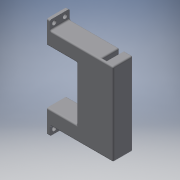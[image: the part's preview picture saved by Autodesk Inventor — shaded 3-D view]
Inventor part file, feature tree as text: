
AUTODESK INVENTOR PART (.ipt)
format: ipt  version: 2018 (Build 220112000, 112)  size: 440,320 bytes
history: native  units: in
note: dims shown in document units (in); Inventor stores cm internally (conversion verified against a paired STEP export)
features: reference x20, extrude x10, sketch x10, other x10, fillet x8, projected_geometry x4, plane x3
ambient origin geometry x8: Origin, YZ Plane, XZ Plane, XY Plane, X Axis, Y Axis, Z Axis, Center Point
bodies: Solid1 (feature_tree)
feature tree (65):
  extrude  "Extrusion1"  Depth=0.125in
  extrude  "Extrusion2"  Depth=0.4724in TaperAngle=0.0deg
  extrude  "Extrusion3"  Depth=0.2in TaperAngle=0.0deg
  extrude  "Extrusion4"  Depth=0.4in
  extrude  "Extrusion5"  Depth=0.25in
  extrude  "Extrusion6"  Depth=0.0787in TaperAngle=0.0deg
  fillet  "Fillet1"  Radius=0.125in
  fillet  "Fillet4"  Radius=0.1181in
  sketch  "Sketch8"  dims[d19=0.125in d20=0.1181in]
  plane  "Work Plane1"
  extrude  "Extrusion7"  Depth=0.1181in
  sketch  "Sketch9"  dims[d21=1.15in d22=0.0787in d23=0.0in d24=0.0394in d27=0.0394in d28=0.0197in d29=0.0197in]
  plane  "Work Plane2"
  extrude  "Extrusion8"  Depth=0.0394in TaperAngle=0.0deg
  fillet  "Fillet5"  Radius=0.0394in
  fillet  "Fillet6"  Radius=0.0394in
  fillet  "Fillet7"  Radius=0.0197in
  fillet  "Fillet9"  Radius=0.0197in
  sketch  "Sketch10"  dims[d30=1.0in d31=0.0in d32=0.0394in d33=0.0394in d34=1.0in d35=0.0in]
  plane  "Work Plane3"
  extrude  "Extrusion9"  Depth=0.0394in
  fillet  "Fillet10"  Radius=0.0394in
  fillet  "Fillet11"  Radius=1.0in
  extrude  "Extrusion12"  Depth=0.0394in
  sketch  "Sketch1"  dims[d0=0.5in d1=0.125in]
  reference  "Reference1"
  reference  "Reference2"
  reference  "Reference3"
  reference  "Reference4"
  reference  "Reference5"
  reference  "Reference6"
  reference  "Reference7"
  reference  "Reference8"
  reference  "Reference9"
  reference  "Reference10"
  reference  "Reference11"
  reference  "Reference12"
  reference  "Reference13"
  reference  "Reference14"
  reference  "Reference15"
  reference  "Reference16"
  reference  "Reference17"
  sketch  "Sketch2"  dims[d2=0.7in d3=0.4724in d4=0.0in]
  projected_geometry  "Projected Loop1"
  projected_geometry  "Projected Loop2"
  sketch  "Sketch4"  dims[d5=0.0787in d6=0.0in d7=0.2in d8=0.0in]
  projected_geometry  "Projected Loop3"
  sketch  "Sketch5"  dims[d9=0.4in d10=0.4in]
  reference  "Reference20"
  sketch  "Sketch6"  dims[d11=0.5512in d12=0.0in d13=0.25in]
  sketch  "Sketch7"  dims[d14=0.25in d15=0.0787in d16=0.0in d17=0.125in d18=0.1181in]
  projected_geometry  "Projected Loop4"
  sketch  "Sketch13"  dims[d36=0.0394in d37=0.0394in d38=0.0394in d40=0.0394in d41=0.0098in d42=1.0in d43=0.0in d44=0.0394in d45=0.0394in d50=0.128in d51=0.128in d52=0.315in d53=0.0in]
  reference  "Reference21"
  reference  "Reference22"
  other  "<userpath>\OneDrive\Documents\Inventor\TSA\2018\Animatronics\Tortoise\TurtleAssembly.iam"
  other  "TurtleAssembly.iam"
  other  "servo (2):1"
  other  "smallergear:4"
  other  "<userpath>\OneDrive\Documents\Inventor\TSA\2018\Animatronics\Tortoise\AssemblyTURTLE.iam"
  other  "AssemblyTURTLE.iam"
  other  "Frame:1"
  other  "<userpath>\OneDrive\Documents\Inventor\TSA\2018\Animatronics\Tortoise\TurtleAssembly2.iam"
  other  "TurtleAssembly2.iam"
  other  "SteerServoClamp:1"
